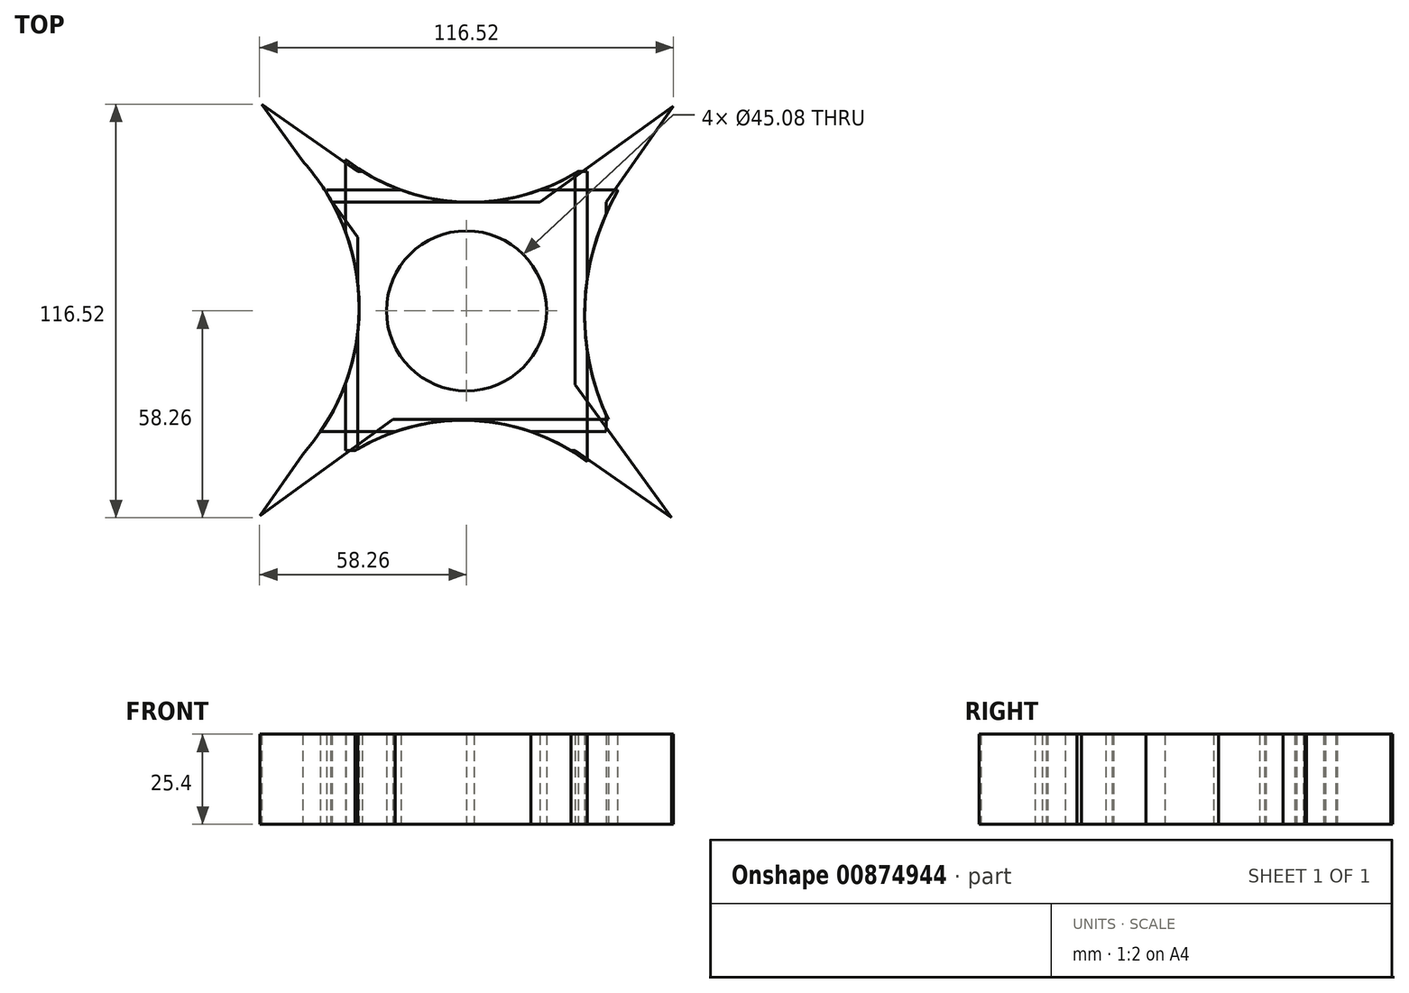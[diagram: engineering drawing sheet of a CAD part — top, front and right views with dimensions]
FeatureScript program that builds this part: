
annotation { "Feature Type Name" : "Feature", "Feature Type Description" : "" }
export const myFeature = defineFeature(function(context is Context, id is Id, definition is map)
    precondition{}
    {
        {
            var Q0;
            Q0=qCreatedBy(makeId("Top.planeOp"),FACE);
            var sketch = newSketch(context, id + "F0", { "sketchPlane" : qUnion([Q0])});
            skCircle(sketch, "E0", {"center": v(0, 0) * mm, "radius": 22.54 * mm});
            skLineSegment(sketch, "E1.bottom", {"start": v(-39.34, 34.03) * mm, "end": v(42.56, 34.03) * mm});
            skLineSegment(sketch, "E1.top", {"start": v(-39.34, -30.62) * mm, "end": v(42.56, -30.62) * mm});
            skLineSegment(sketch, "E1.left", {"start": v(-39.34, 34.03) * mm, "end": v(-39.34, -30.62) * mm});
            skLineSegment(sketch, "E1.right", {"start": v(42.56, 34.03) * mm, "end": v(42.56, -30.62) * mm});
            skLineSegment(sketch, "E2", {"start": v(-39.34, -30.62) * mm, "end": v(-58.26, -57.73) * mm});
            skLineSegment(sketch, "E3", {"start": v(-58.26, -57.73) * mm, "end": v(-20.72, -30.62) * mm});
            skSolve(sketch);
        }
        {
            var Q0;
            Q0=makeQuery(id+"F0.imprint","IMPRINT",FACE,{"disambiguationData":[TD([[makeQuery(id+"F0.imprint","IMPRINT",EDGE,{"derivedFrom":sQuery(id+"F0.wireOp",EDGE,"E0")}),-1.0]])]});
            extrude(context, id + "F1", {"entities" : qUnion([Q0]), "depth" : 25.4 * mm, "offsetDistance" : 25.4 * mm});
        }
        {
            var Q0;
            {var subQ0=sQuery(id+"F0.wireOp",EDGE,"E2");Q0=makeQuery(id+"F0.imprint","IMPRINT",FACE,{"disambiguationData":[TD([[makeQuery(id+"F0.imprint","IMPRINT",EDGE,{"derivedFrom":subQ0}),1.0]])]});}
            extrude(context, id + "F2", {"entities" : qUnion([Q0]), "operationType" : NewBodyOperationType.ADD, "depth" : 25.4 * mm, "offsetDistance" : 25.4 * mm});
        }
        {
            var Q0;
            Q0=qCreatedBy(makeId("Front.planeOp"),FACE);
            var sketch = newSketch(context, id + "F3", { "sketchPlane" : qUnion([Q0])});
            skLineSegment(sketch, "E4", {"start": v(0, 0) * mm, "end": v(0, 24.74) * mm});
            skLineSegment(sketch, "E5", {"start": v(-22.52, 24.74) * mm, "end": v(22.59, 24.74) * mm});
            skSolve(sketch);
        }
        {
            var Q0;
            Q0=makeQuery(id+"F1.opExtrude","SWEPT_BODY",BODY,{"disambiguationData":[OSD([sQuery(id+"F0.wireOp",EDGE,"E0"),sQuery(id+"F0.wireOp",EDGE,"E1.bottom"),sQuery(id+"F0.wireOp",EDGE,"E1.top"),sQuery(id+"F0.wireOp",EDGE,"E1.left"),sQuery(id+"F0.wireOp",EDGE,"E1.right")])]});
            var Q1;
            Q1=sQuery(id+"F3.wireOp",EDGE,"E4");
            circularPattern(context, id + "F4", {"entities" : qUnion([Q0]), "axis" : qUnion([Q1]), "angle" : 360 * degree, "instanceCount" : 4, "equalSpace" : true});
        }
        {
            var Q0;
            Q0=qCreatedBy(makeId("Top.planeOp"),FACE);
            var sketch = newSketch(context, id + "F5", { "sketchPlane" : qUnion([Q0])});
            skCircle(sketch, "E6", {"center": v(1.1, 87.97) * mm, "radius": 57.36 * mm});
            skPoint(sketch, "E6.first.point", {"position": v(-46.55, 56.03) * mm});
            skPoint(sketch, "E6.second.point", {"position": v(0, 30.62) * mm});
            skPoint(sketch, "E6.third.point", {"position": v(47.68, 54.5) * mm});
            skCircle(sketch, "E7", {"center": v(-91.8, 0.92) * mm, "radius": 61.56 * mm});
            skPoint(sketch, "E7.first.point", {"position": v(-60.2, 53.75) * mm});
            skPoint(sketch, "E7.second.point", {"position": v(-30.24, 0) * mm});
            skPoint(sketch, "E7.third.point", {"position": v(-47.11, -41.43) * mm});
            skCircle(sketch, "E8", {"center": v(102.53, -1) * mm, "radius": 69.26 * mm});
            skPoint(sketch, "E8.first.point", {"position": v(33.27, 0) * mm});
            skPoint(sketch, "E8.second.point", {"position": v(63.23, 56.03) * mm});
            skPoint(sketch, "E8.third.point", {"position": v(64.75, -59.06) * mm});
            skCircle(sketch, "E9", {"center": v(-0.97, -89.14) * mm, "radius": 58.34 * mm});
            skPoint(sketch, "E9.first.point", {"position": v(0, -30.8) * mm});
            skPoint(sketch, "E9.second.point", {"position": v(-49.77, -57.16) * mm});
            skPoint(sketch, "E9.third.point", {"position": v(50.72, -62.1) * mm});
            skSolve(sketch);
        }
        {
            var Q0;
            Q0 = qSketchRegion(id + "F5", true);
            extrude(context, id + "F6", {"entities" : qUnion([Q0]), "operationType" : NewBodyOperationType.REMOVE, "depth" : 25.4 * mm, "offsetDistance" : 25.4 * mm});
        }
    });
